# Revit family: Thorn AXYL GEO
name_source: partatom
category: Lighting Fixtures
units: mm (PartAtom-declared; Revit-internal decimal feet)

## family parameters
Always vertical = Yes
Cut with Voids When Loaded = No
Light Source = Yes
Maintain Annotation Orientation = No
OmniClass Number = 23.80.70.00
OmniClass Title = Lighting
Part Type = Normal
Room Calculation Point = No
Round Connector Dimension = Use Diameter
Shared = No
Work Plane-Based = No

## types (1)
- Thorn AXYL GEO
    A = 120 mm  [stored 0.393701 ft]
    Apparent Load = 16 VA
    Assembly Code = Pr_70_70_48_73
    Color Filter = 16777215
    Default Elevation = 0 mm  [stored 0 ft]
    Description = Road and amenity lighing luminaires
    Dimming Lamp Color Temperature Shift = <None>
    Export Type to IFC As = IfcLightFixtureType
    H 600 = Yes
    H 950 = No
    Lamp = LED
    Luminaire Height = 600 mm
    Luminaire Width = 120 mm  [stored 0.393701 ft]
    Manufacturer = Thorn Lighting
    Material Housing = Thorn-Aluminium-RAL 7016-Anthracite Grey
    Model = 96700511
    Photometric Web File = 96700511_(STD).IES
    Power Factor = 0.96
    Tilt Angle = 90.00°
    Type IFC Predefined Type = DIRECTIONSOURCE
    Type Image = TLG_AXYL_F_GEO_H600_ANT.jpg
    URL = https://www.thornlighting.com

note: [stored X ft] marks values corroborated as IEEE doubles in the binary element streams (Revit-internal decimal feet)

## geometry (parser evidence)
native form markers: Sweep x4
no freeform markers — native parametric forms only
